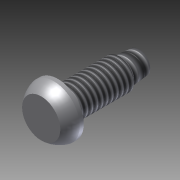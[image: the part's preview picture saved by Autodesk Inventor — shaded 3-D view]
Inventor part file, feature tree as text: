
AUTODESK INVENTOR PART (.ipt)
format: ipt  version: 2011 (Build 150239000, 239)  size: 137,728 bytes
history: native  units: in
note: dims shown in document units (in); Inventor stores cm internally (conversion verified against a paired STEP export)
features: thread x4, imported_body x1
ambient origin geometry x8: Origin, YZ Plane, XZ Plane, XY Plane, X Axis, Y Axis, Z Axis, Center Point
bodies: Solid1 (feature_tree)
feature tree (5):
  imported_body  "Base1"
  thread  "Thread1"  [1 undecoded]
  thread  "Thread2"  [1 undecoded]
  thread  "Thread3"  [1 undecoded]
  thread  "Thread4"  [1 undecoded]
note: 4 required parameter values undecoded (feature->parameter linkage not recoverable at this tier; creation-order binding heuristic only, values carry confidence <= 0.55)
